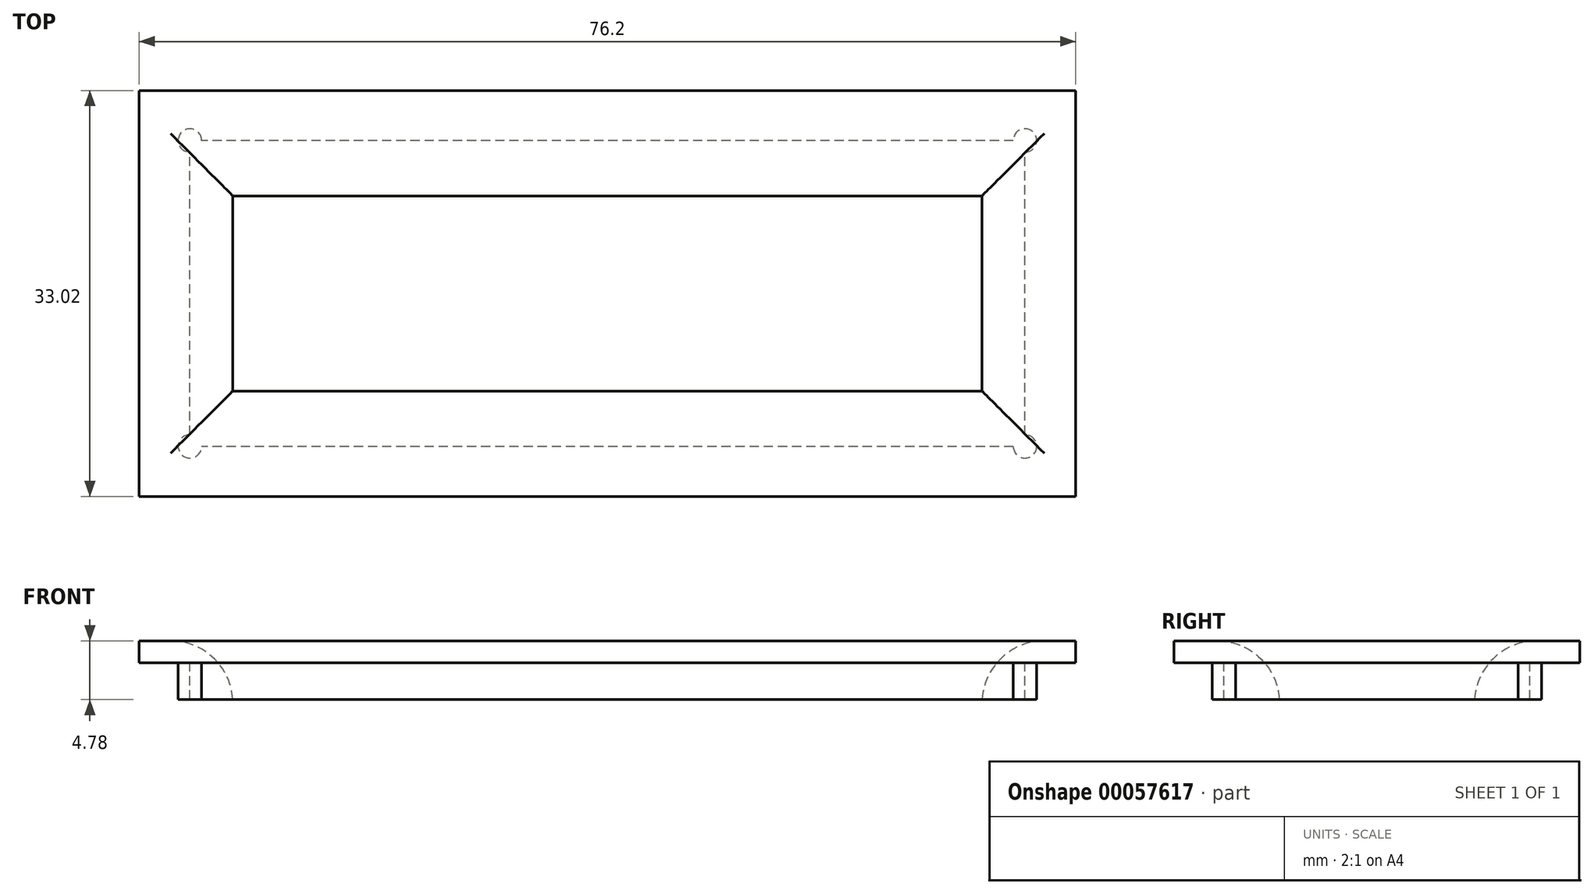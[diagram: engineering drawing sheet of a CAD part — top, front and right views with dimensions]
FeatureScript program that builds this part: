
annotation { "Feature Type Name" : "Feature", "Feature Type Description" : "" }
export const myFeature = defineFeature(function(context is Context, id is Id, definition is map)
    precondition{}
    {
        {
            var Q0;
            Q0=qCreatedBy(makeId("Top.planeOp"),FACE);
            var sketch = newSketch(context, id + "F0", { "sketchPlane" : qUnion([Q0])});
            skLineSegment(sketch, "E0.rect.bottom", {"start": v(30.48, -7.94) * mm, "end": v(-30.48, -7.94) * mm});
            skLineSegment(sketch, "E0.rect.top", {"start": v(30.48, 7.94) * mm, "end": v(-30.48, 7.94) * mm});
            skLineSegment(sketch, "E0.rect.left", {"start": v(30.48, -7.94) * mm, "end": v(30.48, 7.94) * mm});
            skLineSegment(sketch, "E0.rect.right", {"start": v(-30.48, -7.94) * mm, "end": v(-30.48, 7.94) * mm});
            skPoint(sketch, "E0.rect.middle", {"position": v(0, 0) * mm});
            skLineSegment(sketch, "E1.rect.bottom", {"start": v(33.97, -12.45) * mm, "end": v(-33.97, -12.45) * mm});
            skLineSegment(sketch, "E1.rect.top", {"start": v(33.97, 12.45) * mm, "end": v(-33.97, 12.45) * mm});
            skLineSegment(sketch, "E1.rect.left", {"start": v(33.97, -12.45) * mm, "end": v(33.97, 12.45) * mm});
            skLineSegment(sketch, "E1.rect.right", {"start": v(-33.97, -12.45) * mm, "end": v(-33.97, 12.45) * mm});
            skLineSegment(sketch, "E2.rect.bottom", {"start": v(38.1, -16.51) * mm, "end": v(-38.1, -16.51) * mm});
            skLineSegment(sketch, "E2.rect.top", {"start": v(38.1, 16.51) * mm, "end": v(-38.1, 16.51) * mm});
            skLineSegment(sketch, "E2.rect.left", {"start": v(38.1, -16.51) * mm, "end": v(38.1, 16.51) * mm});
            skLineSegment(sketch, "E2.rect.right", {"start": v(-38.1, -16.51) * mm, "end": v(-38.1, 16.51) * mm});
            skArc(sketch, "E3", {"start": v(33.97, 11.5) * mm, "mid": v(34.65, 13.12) * mm, "end": v(33.02, 12.45) * mm});
            skArc(sketch, "E4", {"start": v(-33.02, 12.45) * mm, "mid": v(-34.65, 13.12) * mm, "end": v(-33.97, 11.5) * mm});
            skArc(sketch, "E5", {"start": v(-33.97, -11.5) * mm, "mid": v(-34.65, -13.12) * mm, "end": v(-33.02, -12.45) * mm});
            skArc(sketch, "E6", {"start": v(33.02, -12.45) * mm, "mid": v(34.65, -13.12) * mm, "end": v(33.97, -11.5) * mm});
            skSolve(sketch);
        }
        {
            var Q0;
            Q0=makeQuery(id+"F0.imprint","IMPRINT",FACE,{"disambiguationData":[TD([[makeQuery(id+"F0.imprint","IMPRINT",EDGE,{"derivedFrom":sQuery(id+"F0.wireOp",EDGE,"E0.rect.bottom")}),1.0]])]});
            var Q1;
            {var subQ3=sQuery(id+"F0.wireOp",EDGE,"E3");Q1=makeQuery(id+"F0.imprint","IMPRINT",FACE,{"disambiguationData":[TD([[makeQuery(id+"F0.imprint","IMPRINT",EDGE,{"derivedFrom":subQ3}),1.0]])]});}
            var Q2;
            {var subQ3=sQuery(id+"F0.wireOp",EDGE,"E6");Q2=makeQuery(id+"F0.imprint","IMPRINT",FACE,{"disambiguationData":[TD([[makeQuery(id+"F0.imprint","IMPRINT",EDGE,{"derivedFrom":subQ3}),1.0]])]});}
            var Q3;
            {var subQ3=sQuery(id+"F0.wireOp",EDGE,"E4");Q3=makeQuery(id+"F0.imprint","IMPRINT",FACE,{"disambiguationData":[TD([[makeQuery(id+"F0.imprint","IMPRINT",EDGE,{"derivedFrom":subQ3}),1.0]])]});}
            var Q4;
            {var subQ3=sQuery(id+"F0.wireOp",EDGE,"E5");Q4=makeQuery(id+"F0.imprint","IMPRINT",FACE,{"disambiguationData":[TD([[makeQuery(id+"F0.imprint","IMPRINT",EDGE,{"derivedFrom":subQ3}),1.0]])]});}
            extrude(context, id + "F1", {"entities" : qUnion([Q0, Q1, Q2, Q3, Q4]), "depth" : 4.78 * mm});
        }
        {
            var Q0;
            Q0=makeQuery(id+"F0.imprint","IMPRINT",FACE,{"disambiguationData":[TD([[makeQuery(id+"F0.imprint","IMPRINT",EDGE,{"derivedFrom":sQuery(id+"F0.wireOp",EDGE,"E2.rect.bottom")}),-1.0]])]});
            extrude(context, id + "F2", {"entities" : qUnion([Q0]), "operationType" : NewBodyOperationType.ADD, "depth" : 1.78 * mm});
        }
        {
            var Q0;
            Q0=makeQuery(id+"F1.opExtrude","CAP_EDGE",EDGE,{"disambiguationData":[OSD([sQuery(id+"F0.wireOp",EDGE,"E0.rect.bottom")])],"isStart":true});
            var Q1;
            Q1=makeQuery(id+"F1.opExtrude","CAP_EDGE",EDGE,{"disambiguationData":[OSD([sQuery(id+"F0.wireOp",EDGE,"E0.rect.left")])],"isStart":true});
            var Q2;
            Q2=makeQuery(id+"F1.opExtrude","CAP_EDGE",EDGE,{"disambiguationData":[OSD([sQuery(id+"F0.wireOp",EDGE,"E0.rect.top")])],"isStart":true});
            var Q3;
            Q3=makeQuery(id+"F1.opExtrude","CAP_EDGE",EDGE,{"disambiguationData":[OSD([sQuery(id+"F0.wireOp",EDGE,"E0.rect.right")])],"isStart":true});
            fillet(context, id + "F3", {"entities" : qUnion([Q0, Q1, Q2, Q3]), "radius" : 5.08 * mm, "tangentPropagation" : true, "allowEdgeOverflow" : false});
        }
        {
            var Q0;
            Q0=makeQuery(id+"F1.opExtrude","SWEPT_BODY",BODY,{"disambiguationData":[OSD([sQuery(id+"F0.wireOp",EDGE,"E0.rect.bottom"),sQuery(id+"F0.wireOp",EDGE,"E0.rect.top"),sQuery(id+"F0.wireOp",EDGE,"E0.rect.left"),sQuery(id+"F0.wireOp",EDGE,"E0.rect.right"),sQuery(id+"F0.wireOp",EDGE,"E1.rect.bottom"),sQuery(id+"F0.wireOp",EDGE,"E1.rect.top"),sQuery(id+"F0.wireOp",EDGE,"E1.rect.left"),sQuery(id+"F0.wireOp",EDGE,"E1.rect.right"),sQuery(id+"F0.wireOp",EDGE,"E3"),sQuery(id+"F0.wireOp",EDGE,"E4"),sQuery(id+"F0.wireOp",EDGE,"E5"),sQuery(id+"F0.wireOp",EDGE,"E6")])]});
            var Q1;
            Q1=qCreatedBy(makeId("Top.planeOp"),FACE);
            mirror(context, id + "F4", {"entities" : qUnion([Q0]), "mirrorPlane" : qUnion([Q1])});
        }
        {
            var Q0;
            Q0=makeQuery(id+"F1.opExtrude","SWEPT_BODY",BODY,{"disambiguationData":[OSD([sQuery(id+"F0.wireOp",EDGE,"E0.rect.bottom"),sQuery(id+"F0.wireOp",EDGE,"E0.rect.top"),sQuery(id+"F0.wireOp",EDGE,"E0.rect.left"),sQuery(id+"F0.wireOp",EDGE,"E0.rect.right"),sQuery(id+"F0.wireOp",EDGE,"E1.rect.bottom"),sQuery(id+"F0.wireOp",EDGE,"E1.rect.top"),sQuery(id+"F0.wireOp",EDGE,"E1.rect.left"),sQuery(id+"F0.wireOp",EDGE,"E1.rect.right"),sQuery(id+"F0.wireOp",EDGE,"E3"),sQuery(id+"F0.wireOp",EDGE,"E4"),sQuery(id+"F0.wireOp",EDGE,"E5"),sQuery(id+"F0.wireOp",EDGE,"E6")])]});
            deleteBodies(context, id + "F5", {"entities" : qUnion([Q0])});
        }
    });
